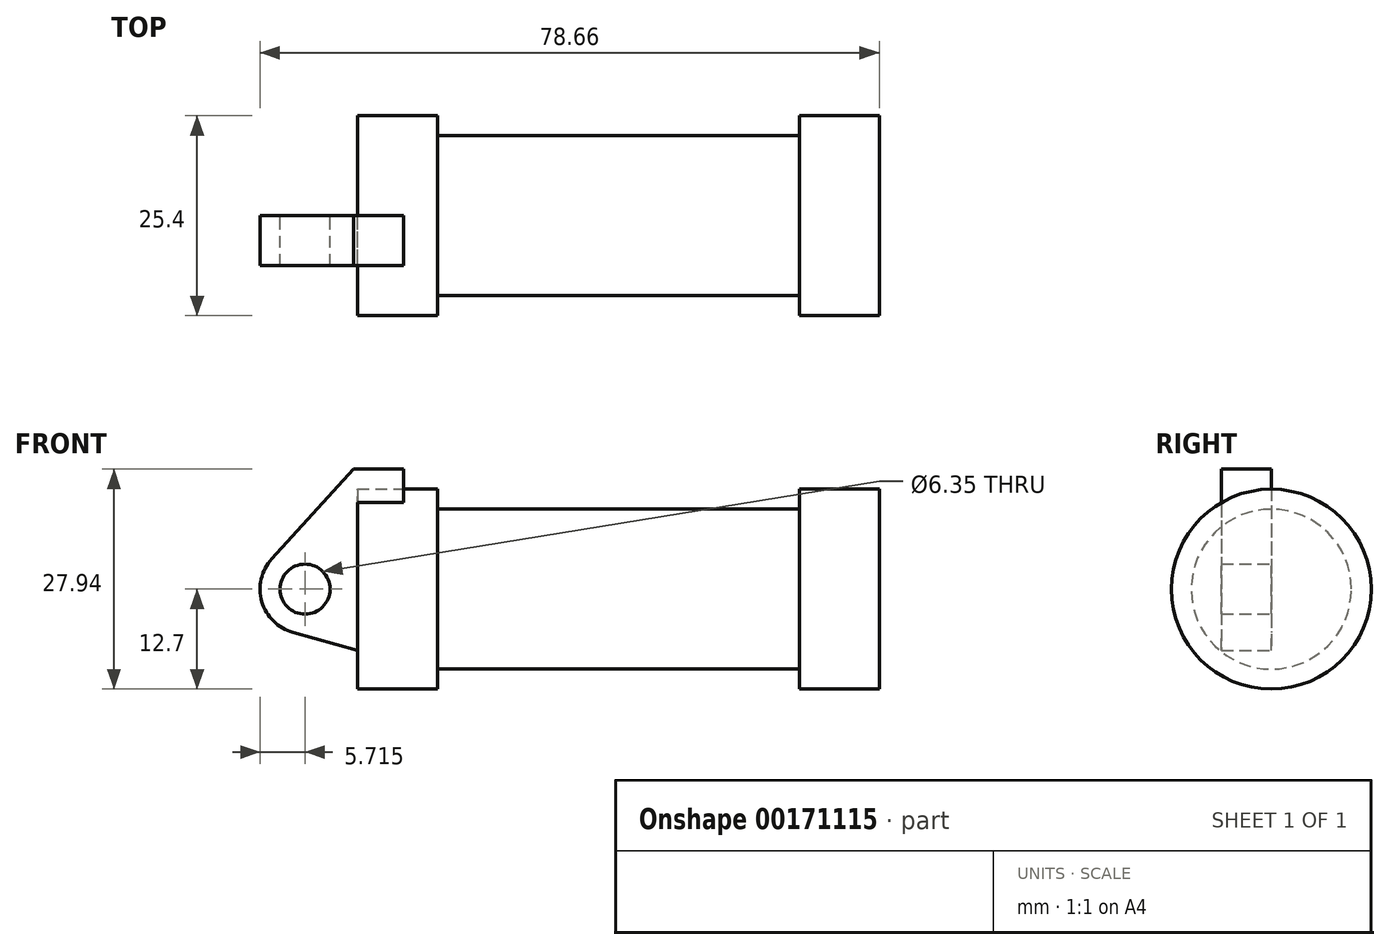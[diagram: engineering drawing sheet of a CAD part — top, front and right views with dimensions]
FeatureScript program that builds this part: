
annotation { "Feature Type Name" : "Feature", "Feature Type Description" : "" }
export const myFeature = defineFeature(function(context is Context, id is Id, definition is map)
    precondition{}
    {
        {
            var Q0;
            Q0=qCreatedBy(makeId("Front.planeOp"),FACE);
            var sketch = newSketch(context, id + "F0", { "sketchPlane" : qUnion([Q0])});
            skLineSegment(sketch, "E0", {"start": v(0, 0) * mm, "end": v(0, 12.7) * mm});
            skLineSegment(sketch, "E1", {"start": v(0, 12.7) * mm, "end": v(10.16, 12.7) * mm});
            skLineSegment(sketch, "E2", {"start": v(10.16, 12.7) * mm, "end": v(10.16, 10.16) * mm});
            skLineSegment(sketch, "E3", {"start": v(10.16, 10.16) * mm, "end": v(56.13, 10.16) * mm});
            skLineSegment(sketch, "E4", {"start": v(56.13, 10.16) * mm, "end": v(56.13, 12.7) * mm});
            skLineSegment(sketch, "E5", {"start": v(56.13, 12.7) * mm, "end": v(66.3, 12.7) * mm});
            skLineSegment(sketch, "E6", {"start": v(66.3, 12.7) * mm, "end": v(66.3, 0) * mm});
            skLineSegment(sketch, "E7", {"start": v(66.3, 0) * mm, "end": v(0, 0) * mm});
            skLineSegment(sketch, "E8", {"start": v(5.84, 15.24) * mm, "end": v(-0.5, 15.24) * mm});
            skLineSegment(sketch, "E9", {"start": v(-0.5, 15.24) * mm, "end": v(-10.88, 3.85) * mm});
            skLineSegment(sketch, "E10", {"start": v(0, 0) * mm, "end": v(-6.65, 0) * mm});
            skCircle(sketch, "E11", {"center": v(-6.65, 0) * mm, "radius": 5.72 * mm});
            skCircle(sketch, "E12", {"center": v(-6.65, 0) * mm, "radius": 3.18 * mm});
            skLineSegment(sketch, "E13", {"start": v(5.84, 15.24) * mm, "end": v(5.84, -9.4) * mm});
            skLineSegment(sketch, "E14", {"start": v(5.84, -9.4) * mm, "end": v(-8.18, -5.5) * mm});
            skSolve(sketch);
        }
        {
            var Q0;
            {var subQ0=sQuery(id+"F0.wireOp",EDGE,"E2");Q0=makeQuery(id+"F0.imprint","IMPRINT",FACE,{"disambiguationData":[TD([[makeQuery(id+"F0.imprint","IMPRINT",EDGE,{"derivedFrom":subQ0}),-1.0]])]});}
            var Q1;
            {var subQ0=sQuery(id+"F0.wireOp",EDGE,"E0");Q1=makeQuery(id+"F0.imprint","IMPRINT",FACE,{"disambiguationData":[TD([[makeQuery(id+"F0.imprint","IMPRINT",EDGE,{"derivedFrom":subQ0}),-1.0]])]});}
            var Q2;
            Q2=sQuery(id+"F0.wireOp",EDGE,"E7");
            var Q3;
            Q3=sQuery(id+"F0.wireOp",EDGE,"E7");
            revolve(context, id + "F1", {"entities" : qUnion([Q0, Q1]), "surfaceEntities" : qUnion([Q2]), "axis" : qUnion([Q3]), "revolveType" : RevolveType.FULL});
        }
        {
            var Q0;
            {var subQ3=sQuery(id+"F0.wireOp",EDGE,"E0");Q0=makeQuery(id+"F0.imprint","IMPRINT",FACE,{"disambiguationData":[TD([[makeQuery(id+"F0.imprint","IMPRINT",EDGE,{"derivedFrom":subQ3}),1.0]])]});}
            var Q1;
            {var subQ0=sQuery(id+"F0.wireOp",EDGE,"E14");Q1=makeQuery(id+"F0.imprint","IMPRINT",FACE,{"disambiguationData":[TD([[makeQuery(id+"F0.imprint","IMPRINT",EDGE,{"derivedFrom":subQ0}),-1.0]])]});}
            var Q2;
            {var subQ4=sQuery(id+"F0.wireOp",EDGE,"E12");Q2=makeQuery(id+"F0.imprint","IMPRINT",FACE,{"disambiguationData":[TD([[makeQuery(id+"F0.imprint","IMPRINT",EDGE,{"derivedFrom":subQ4}),-1.0]])]});}
            var Q3;
            {var subQ0=sQuery(id+"F0.wireOp",EDGE,"E0");Q3=makeQuery(id+"F0.imprint","IMPRINT",FACE,{"disambiguationData":[TD([[makeQuery(id+"F0.imprint","IMPRINT",EDGE,{"derivedFrom":subQ0}),-1.0]])]});}
            extrude(context, id + "F2", {"entities" : qUnion([Q0, Q1, Q2, Q3]), "operationType" : NewBodyOperationType.ADD, "depth" : 6.35 * mm});
        }
    });
